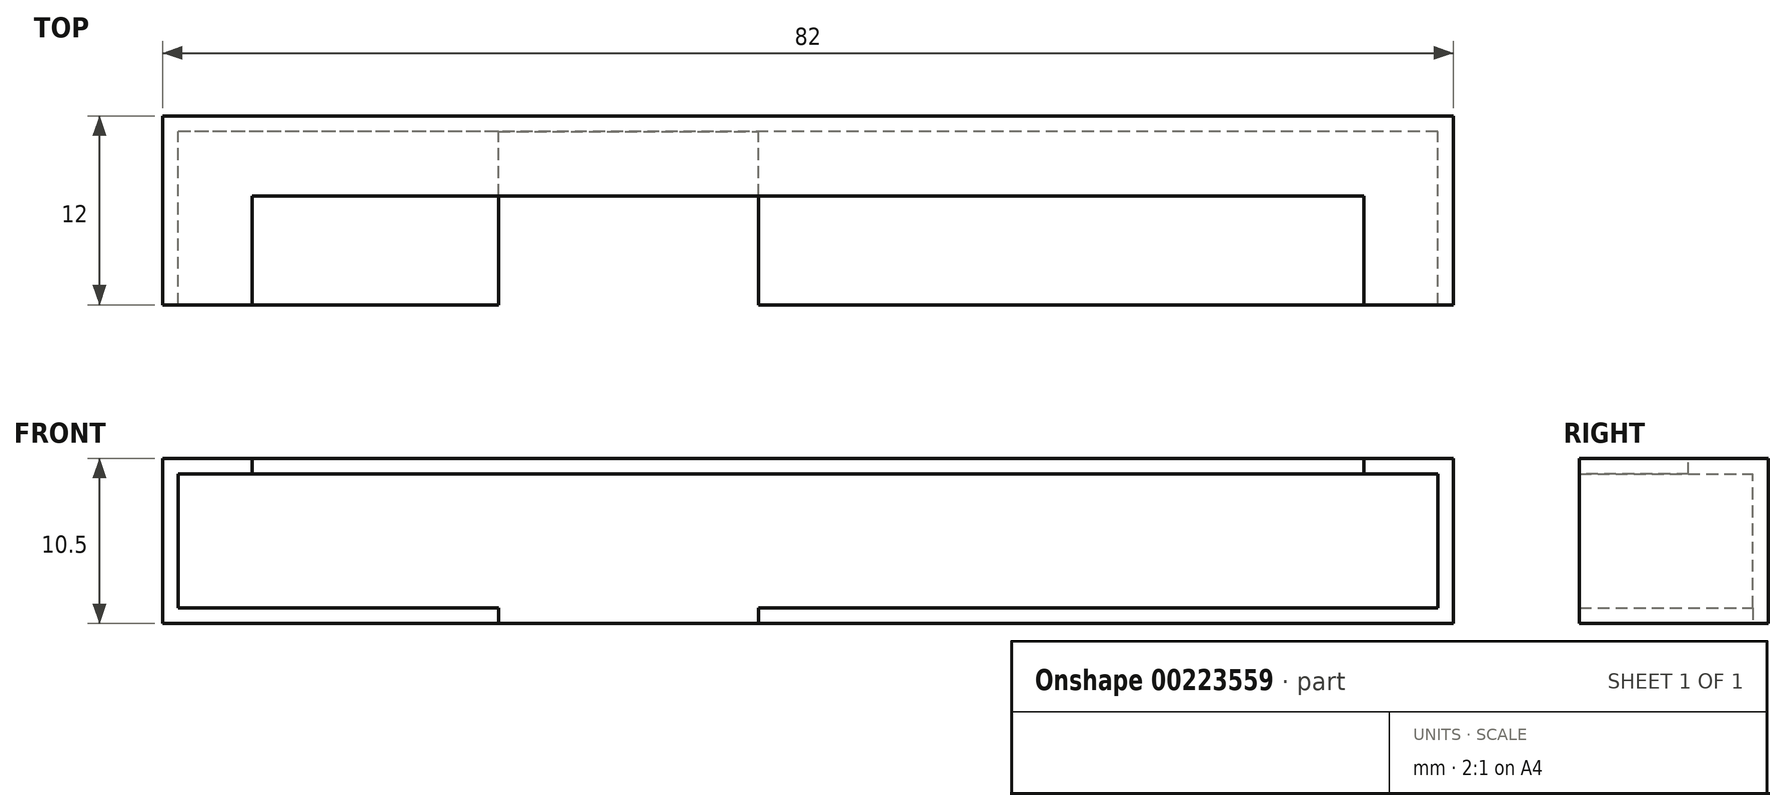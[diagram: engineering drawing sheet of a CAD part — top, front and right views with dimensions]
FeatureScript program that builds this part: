
annotation { "Feature Type Name" : "Feature", "Feature Type Description" : "" }
export const myFeature = defineFeature(function(context is Context, id is Id, definition is map)
    precondition{}
    {
        {
            var Q0;
            Q0=qCreatedBy(makeId("Front.planeOp"),FACE);
            var sketch = newSketch(context, id + "F0", { "sketchPlane" : qUnion([Q0])});
            skLineSegment(sketch, "E0.bottom", {"start": v(41, -5.25) * mm, "end": v(-41, -5.25) * mm});
            skLineSegment(sketch, "E0.top", {"start": v(41, 5.25) * mm, "end": v(-41, 5.25) * mm});
            skLineSegment(sketch, "E0.left", {"start": v(41, -5.25) * mm, "end": v(41, 5.25) * mm});
            skLineSegment(sketch, "E0.right", {"start": v(-41, -5.25) * mm, "end": v(-41, 5.25) * mm});
            skPoint(sketch, "E0.middle", {"position": v(0, 0) * mm});
            skSolve(sketch);
        }
        {
            var Q0;
            Q0=makeQuery(id+"F0.imprint","IMPRINT",FACE,{"disambiguationData":[TD([[makeQuery(id+"F0.imprint","IMPRINT",EDGE,{"derivedFrom":sQuery(id+"F0.wireOp",EDGE,"E0.bottom")}),-1.0]])]});
            extrude(context, id + "F1", {"entities" : qUnion([Q0]), "depth" : 12 * mm});
        }
        {
            var Q0;
            Q0=makeQuery(id+"F1.opExtrude","CAP_FACE",FACE,{"disambiguationData":[OSD([sQuery(id+"F0.wireOp",EDGE,"E0.bottom"),sQuery(id+"F0.wireOp",EDGE,"E0.top"),sQuery(id+"F0.wireOp",EDGE,"E0.left"),sQuery(id+"F0.wireOp",EDGE,"E0.right")])],"isStart":false});
            shell(context, id + "F2", {"entities" : qUnion([Q0]), "thickness" : 1 * mm});
        }
        {
            var Q0;
            Q0=makeQuery(id+"F1.opExtrude","SWEPT_FACE",FACE,{"disambiguationData":[OSD([sQuery(id+"F0.wireOp",EDGE,"E0.bottom")])]});
            var sketch = newSketch(context, id + "F3", { "sketchPlane" : qUnion([Q0])});
            skLineSegment(sketch, "E1.bottom", {"start": v(-19.66, 12) * mm, "end": v(-3.15, 12) * mm});
            skLineSegment(sketch, "E1.top", {"start": v(-19.66, 1) * mm, "end": v(-3.15, 1) * mm});
            skLineSegment(sketch, "E1.left", {"start": v(-19.66, 12) * mm, "end": v(-19.66, 1) * mm});
            skLineSegment(sketch, "E1.right", {"start": v(-3.15, 12) * mm, "end": v(-3.15, 1) * mm});
            skSolve(sketch);
        }
        {
            var Q0;
            Q0=makeQuery(id+"F3.imprint","IMPRINT",FACE,{"disambiguationData":[TD([[makeQuery(id+"F3.imprint","IMPRINT",EDGE,{"derivedFrom":sQuery(id+"F3.wireOp",EDGE,"E1.bottom")}),1.0]])]});
            extrude(context, id + "F4", {"entities" : qUnion([Q0]), "operationType" : NewBodyOperationType.REMOVE, "oppositeDirection" : true, "depth" : 1 * mm});
        }
        {
            var Q0;
            Q0=makeQuery(id+"F1.opExtrude","SWEPT_FACE",FACE,{"disambiguationData":[OSD([sQuery(id+"F0.wireOp",EDGE,"E0.top")])]});
            var sketch = newSketch(context, id + "F5", { "sketchPlane" : qUnion([Q0])});
            skLineSegment(sketch, "E2", {"start": v(-35.3, -12) * mm, "end": v(-35.3, -5.08) * mm});
            skLineSegment(sketch, "E3", {"start": v(-35.3, -5.08) * mm, "end": v(35.3, -5.08) * mm});
            skLineSegment(sketch, "E4", {"start": v(35.3, -5.08) * mm, "end": v(35.3, -12) * mm});
            skLineSegment(sketch, "E5", {"start": v(35.3, -12) * mm, "end": v(-35.3, -12) * mm});
            skSolve(sketch);
        }
        {
            var Q0;
            Q0=makeQuery(id+"F5.imprint","IMPRINT",FACE,{"disambiguationData":[TD([[makeQuery(id+"F5.imprint","IMPRINT",EDGE,{"derivedFrom":sQuery(id+"F5.wireOp",EDGE,"E2")}),-1.0]])]});
            extrude(context, id + "F6", {"entities" : qUnion([Q0]), "operationType" : NewBodyOperationType.REMOVE, "oppositeDirection" : true, "depth" : 2.54 * mm});
        }
    });
